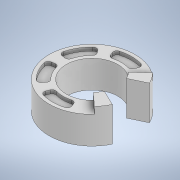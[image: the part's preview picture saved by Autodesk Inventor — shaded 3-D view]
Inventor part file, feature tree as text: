
AUTODESK INVENTOR PART (.ipt)
format: ipt  version: 2021.1 (Build 251245010, 245A)  size: 200,192 bytes
history: native  units: mm
features: extrude x3, sketch x2, other x1, projected_geometry x1
ambient origin geometry x8: Origin, YZ Plane, XZ Plane, XY Plane, X Axis, Y Axis, Z Axis, Center Point
bodies: Body1 (feature_tree)
feature tree (7):
  other  "Твердое тело1"
  extrude  "Выдавливание1"  Depth=25.0mm
  extrude  "Выдавливание2"  Depth=15.0mm
  extrude  "Выдавливание3"  Depth=8.0mm TaperAngle=0.0deg
  sketch  "Эскиз2"
  projected_geometry  "Спроецированная петля1"
  sketch  "Эскиз3"
